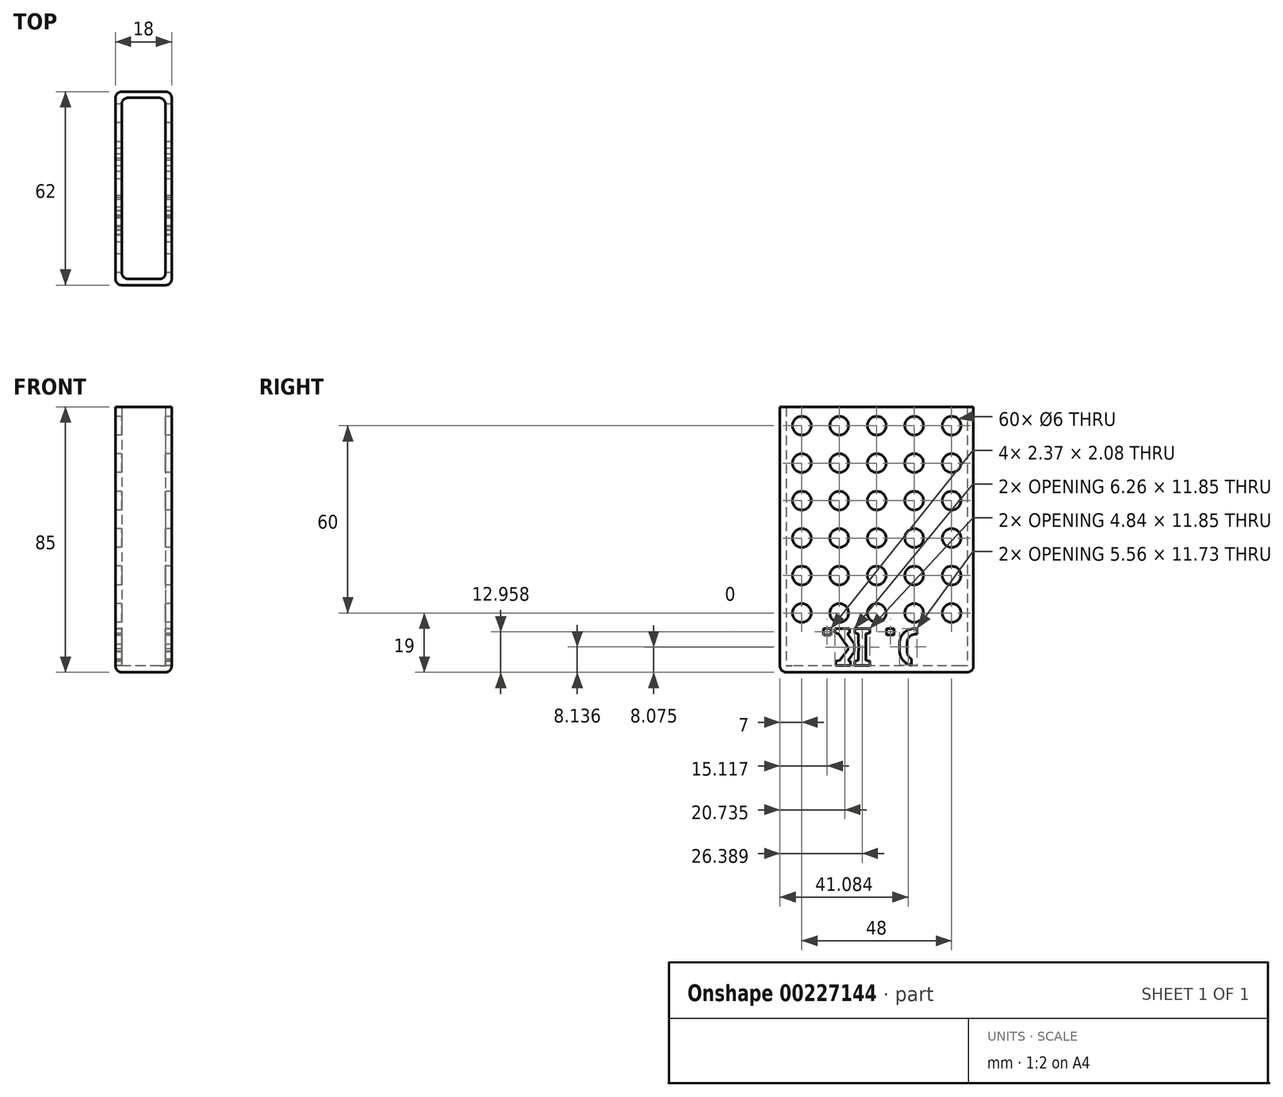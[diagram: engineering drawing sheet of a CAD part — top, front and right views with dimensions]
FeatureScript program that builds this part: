
annotation { "Feature Type Name" : "Feature", "Feature Type Description" : "" }
export const myFeature = defineFeature(function(context is Context, id is Id, definition is map)
    precondition{}
    {
        {
            var Q0;
            Q0=qCreatedBy(makeId("Top.planeOp"),FACE);
            var sketch = newSketch(context, id + "F0", { "sketchPlane" : qUnion([Q0])});
            skLineSegment(sketch, "E0.bottom", {"start": v(7, 31) * mm, "end": v(-7, 31) * mm});
            skLineSegment(sketch, "E0.top", {"start": v(7, -31) * mm, "end": v(-7, -31) * mm});
            skLineSegment(sketch, "E0.left", {"start": v(9, 29) * mm, "end": v(9, -29) * mm});
            skLineSegment(sketch, "E0.right", {"start": v(-9, 29) * mm, "end": v(-9, -29) * mm});
            skPoint(sketch, "E0.middle", {"position": v(0, 0) * mm});
            skPoint(sketch, "E1.visualSharp", {"position": v(9, 31) * mm});
            skArc(sketch, "E1.filletArc", {"start": v(9, 29) * mm, "mid": v(8.41, 30.41) * mm, "end": v(7, 31) * mm});
            skPoint(sketch, "E2.visualSharp", {"position": v(-9, 31) * mm});
            skArc(sketch, "E2.filletArc", {"start": v(-7, 31) * mm, "mid": v(-8.41, 30.41) * mm, "end": v(-9, 29) * mm});
            skPoint(sketch, "E3.visualSharp", {"position": v(-9, -31) * mm});
            skArc(sketch, "E3.filletArc", {"start": v(-9, -29) * mm, "mid": v(-8.41, -30.41) * mm, "end": v(-7, -31) * mm});
            skPoint(sketch, "E4.visualSharp", {"position": v(9, -31) * mm});
            skArc(sketch, "E4.filletArc", {"start": v(7, -31) * mm, "mid": v(8.41, -30.41) * mm, "end": v(9, -29) * mm});
            skLineSegment(sketch, "E5.bottom", {"start": v(5, 29) * mm, "end": v(-5, 29) * mm});
            skLineSegment(sketch, "E5.top", {"start": v(5.2, -29) * mm, "end": v(-5, -29) * mm});
            skLineSegment(sketch, "E5.left", {"start": v(7, 27) * mm, "end": v(7, -27.2) * mm});
            skLineSegment(sketch, "E5.right", {"start": v(-7, 27) * mm, "end": v(-7, -27) * mm});
            skArc(sketch, "E6.filletArc", {"start": v(7, 27) * mm, "mid": v(6.41, 28.41) * mm, "end": v(5, 29) * mm});
            skArc(sketch, "E7.filletArc", {"start": v(-5, 29) * mm, "mid": v(-6.41, 28.41) * mm, "end": v(-7, 27) * mm});
            skArc(sketch, "E8.filletArc", {"start": v(-7, -27) * mm, "mid": v(-6.41, -28.41) * mm, "end": v(-5, -29) * mm});
            skArc(sketch, "E9.filletArc", {"start": v(5.2, -29) * mm, "mid": v(6.47, -28.47) * mm, "end": v(7, -27.2) * mm});
            skSolve(sketch);
        }
        {
            var Q0;
            Q0=makeQuery(id+"F0.imprint","IMPRINT",FACE,{"disambiguationData":[TD([[makeQuery(id+"F0.imprint","IMPRINT",EDGE,{"derivedFrom":sQuery(id+"F0.wireOp",EDGE,"E0.bottom")}),1.0]])]});
            extrude(context, id + "F1", {"entities" : qUnion([Q0]), "depth" : (87 - 4) * mm});
        }
        {
            var Q0;
            Q0=makeQuery(id+"F0.imprint","IMPRINT",FACE,{"disambiguationData":[TD([[makeQuery(id+"F0.imprint","IMPRINT",EDGE,{"derivedFrom":sQuery(id+"F0.wireOp",EDGE,"E0.bottom")}),1.0]])]});
            var Q1;
            Q1=makeQuery(id+"F0.imprint","IMPRINT",FACE,{"disambiguationData":[TD([[makeQuery(id+"F0.imprint","IMPRINT",EDGE,{"derivedFrom":sQuery(id+"F0.wireOp",EDGE,"E5.bottom")}),1.0]])]});
            extrude(context, id + "F2", {"entities" : qUnion([Q0, Q1]), "operationType" : NewBodyOperationType.ADD, "oppositeDirection" : true, "depth" : 2 * mm});
        }
        {
            var Q0;
            Q0=makeQuery(id+"F0.imprint","IMPRINT",FACE,{"disambiguationData":[TD([[makeQuery(id+"F0.imprint","IMPRINT",EDGE,{"derivedFrom":sQuery(id+"F0.wireOp",EDGE,"E0.bottom")}),1.0]])]});
            extrude(context, id + "F3", {"entities" : qUnion([Q0]), "operationType" : NewBodyOperationType.ADD, "oppositeDirection" : true, "depth" : 2 * mm});
        }
        {
            var Q0;
            {var subQ0=sQuery(id+"F0.wireOp",EDGE,"E0.bottom");var subQ1=sQuery(id+"F0.wireOp",EDGE,"E1.filletArc");Q0=makeQuery(id+"FxfuuWBWUbWDivL_1.boolean.opBoolean","SPLIT",EDGE,{"disambiguationData":[TD([makeQuery(id+"F1.opExtrude","SWEPT_FACE",FACE,{"disambiguationData":[OSD([subQ1])]})])],"derivedFrom":makeQuery(id+"F2.opExtrude","CAP_EDGE",EDGE,{"disambiguationData":[OSD([subQ0])],"isStart":false})});}
            fillet(context, id + "F4", {"entities" : qUnion([Q0]), "radius" : 2 * mm, "tangentPropagation" : true, "allowEdgeOverflow" : false});
        }
        {
            var Q0;
            {var subQ0=sQuery(id+"F0.wireOp",EDGE,"E0.right");Q0=makeQuery(id+"F2.boolean.opBoolean","MERGE",FACE,{"derivedFrom":[makeQuery(id+"F1.opExtrude","SWEPT_FACE",FACE,{"disambiguationData":[OSD([subQ0])]}),makeQuery(id+"F2.opExtrude","SWEPT_FACE",FACE,{"disambiguationData":[OSD([subQ0])]})]});}
            var sketch = newSketch(context, id + "F5", { "sketchPlane" : qUnion([Q0])});
            skCircle(sketch, "E10", {"center": v(-24, 77) * mm, "radius": 3 * mm});
            skCircle(sketch, "E11.0.1.0", {"center": v(-24, 65) * mm, "radius": 3 * mm});
            skCircle(sketch, "E11.0.2.0", {"center": v(-24, 53) * mm, "radius": 3 * mm});
            skCircle(sketch, "E11.0.3.0", {"center": v(-24, 41) * mm, "radius": 3 * mm});
            skCircle(sketch, "E11.0.4.0", {"center": v(-24, 29) * mm, "radius": 3 * mm});
            skCircle(sketch, "E11.0.5.0", {"center": v(-24, 17) * mm, "radius": 3 * mm});
            skCircle(sketch, "E11.1.0.0", {"center": v(-12, 77) * mm, "radius": 3 * mm});
            skCircle(sketch, "E11.1.1.0", {"center": v(-12, 65) * mm, "radius": 3 * mm});
            skCircle(sketch, "E11.1.2.0", {"center": v(-12, 53) * mm, "radius": 3 * mm});
            skCircle(sketch, "E11.1.3.0", {"center": v(-12, 41) * mm, "radius": 3 * mm});
            skCircle(sketch, "E11.1.4.0", {"center": v(-12, 29) * mm, "radius": 3 * mm});
            skCircle(sketch, "E11.1.5.0", {"center": v(-12, 17) * mm, "radius": 3 * mm});
            skCircle(sketch, "E11.2.0.0", {"center": v(0, 77) * mm, "radius": 3 * mm});
            skCircle(sketch, "E11.2.1.0", {"center": v(0, 65) * mm, "radius": 3 * mm});
            skCircle(sketch, "E11.2.2.0", {"center": v(0, 53) * mm, "radius": 3 * mm});
            skCircle(sketch, "E11.2.3.0", {"center": v(0, 41) * mm, "radius": 3 * mm});
            skCircle(sketch, "E11.2.4.0", {"center": v(0, 29) * mm, "radius": 3 * mm});
            skCircle(sketch, "E11.2.5.0", {"center": v(0, 17) * mm, "radius": 3 * mm});
            skCircle(sketch, "E11.3.0.0", {"center": v(12, 77) * mm, "radius": 3 * mm});
            skCircle(sketch, "E11.3.1.0", {"center": v(12, 65) * mm, "radius": 3 * mm});
            skCircle(sketch, "E11.3.2.0", {"center": v(12, 53) * mm, "radius": 3 * mm});
            skCircle(sketch, "E11.3.3.0", {"center": v(12, 41) * mm, "radius": 3 * mm});
            skCircle(sketch, "E11.3.4.0", {"center": v(12, 29) * mm, "radius": 3 * mm});
            skCircle(sketch, "E11.3.5.0", {"center": v(12, 17) * mm, "radius": 3 * mm});
            skCircle(sketch, "E11.4.0.0", {"center": v(24, 77) * mm, "radius": 3 * mm});
            skCircle(sketch, "E11.4.1.0", {"center": v(24, 65) * mm, "radius": 3 * mm});
            skCircle(sketch, "E11.4.2.0", {"center": v(24, 53) * mm, "radius": 3 * mm});
            skCircle(sketch, "E11.4.3.0", {"center": v(24, 41) * mm, "radius": 3 * mm});
            skCircle(sketch, "E11.4.4.0", {"center": v(24, 29) * mm, "radius": 3 * mm});
            skCircle(sketch, "E11.4.5.0", {"center": v(24, 17) * mm, "radius": 3 * mm});
            skLineSegment(sketch, "E11.direction1", {"start": v(-24, 77) * mm, "end": v(-12, 77) * mm, "construction": true});
            skLineSegment(sketch, "E11.direction2", {"start": v(-24, 77) * mm, "end": v(-24, 65) * mm, "construction": true});
            skSolve(sketch);
        }
        {
            var Q0;
            Q0=makeQuery(id+"F5.imprint","IMPRINT",FACE,{"disambiguationData":[TD([[makeQuery(id+"F5.imprint","IMPRINT",EDGE,{"derivedFrom":sQuery(id+"F5.wireOp",EDGE,"E10")}),1.0]])]});
            var Q1;
            Q1=makeQuery(id+"F5.imprint","IMPRINT",FACE,{"disambiguationData":[TD([[makeQuery(id+"F5.imprint","IMPRINT",EDGE,{"derivedFrom":sQuery(id+"F5.wireOp",EDGE,"E11.0.5.0")}),1.0]])]});
            var Q2;
            Q2=makeQuery(id+"F5.imprint","IMPRINT",FACE,{"disambiguationData":[TD([[makeQuery(id+"F5.imprint","IMPRINT",EDGE,{"derivedFrom":sQuery(id+"F5.wireOp",EDGE,"E11.1.5.0")}),1.0]])]});
            var Q3;
            Q3=makeQuery(id+"F5.imprint","IMPRINT",FACE,{"disambiguationData":[TD([[makeQuery(id+"F5.imprint","IMPRINT",EDGE,{"derivedFrom":sQuery(id+"F5.wireOp",EDGE,"E11.2.5.0")}),1.0]])]});
            var Q4;
            Q4=makeQuery(id+"F5.imprint","IMPRINT",FACE,{"disambiguationData":[TD([[makeQuery(id+"F5.imprint","IMPRINT",EDGE,{"derivedFrom":sQuery(id+"F5.wireOp",EDGE,"E11.4.5.0")}),1.0]])]});
            var Q5;
            Q5=makeQuery(id+"F5.imprint","IMPRINT",FACE,{"disambiguationData":[TD([[makeQuery(id+"F5.imprint","IMPRINT",EDGE,{"derivedFrom":sQuery(id+"F5.wireOp",EDGE,"E11.4.4.0")}),1.0]])]});
            var Q6;
            Q6=makeQuery(id+"F5.imprint","IMPRINT",FACE,{"disambiguationData":[TD([[makeQuery(id+"F5.imprint","IMPRINT",EDGE,{"derivedFrom":sQuery(id+"F5.wireOp",EDGE,"E11.4.3.0")}),1.0]])]});
            var Q7;
            Q7=makeQuery(id+"F5.imprint","IMPRINT",FACE,{"disambiguationData":[TD([[makeQuery(id+"F5.imprint","IMPRINT",EDGE,{"derivedFrom":sQuery(id+"F5.wireOp",EDGE,"E11.4.2.0")}),1.0]])]});
            var Q8;
            Q8=makeQuery(id+"F5.imprint","IMPRINT",FACE,{"disambiguationData":[TD([[makeQuery(id+"F5.imprint","IMPRINT",EDGE,{"derivedFrom":sQuery(id+"F5.wireOp",EDGE,"E11.4.1.0")}),1.0]])]});
            var Q9;
            Q9=makeQuery(id+"F5.imprint","IMPRINT",FACE,{"disambiguationData":[TD([[makeQuery(id+"F5.imprint","IMPRINT",EDGE,{"derivedFrom":sQuery(id+"F5.wireOp",EDGE,"E11.4.0.0")}),1.0]])]});
            var Q10;
            Q10=makeQuery(id+"F5.imprint","IMPRINT",FACE,{"disambiguationData":[TD([[makeQuery(id+"F5.imprint","IMPRINT",EDGE,{"derivedFrom":sQuery(id+"F5.wireOp",EDGE,"E11.2.0.0")}),1.0]])]});
            var Q11;
            Q11=makeQuery(id+"F5.imprint","IMPRINT",FACE,{"disambiguationData":[TD([[makeQuery(id+"F5.imprint","IMPRINT",EDGE,{"derivedFrom":sQuery(id+"F5.wireOp",EDGE,"E11.1.0.0")}),1.0]])]});
            var Q12;
            Q12=makeQuery(id+"F5.imprint","IMPRINT",FACE,{"disambiguationData":[TD([[makeQuery(id+"F5.imprint","IMPRINT",EDGE,{"derivedFrom":sQuery(id+"F5.wireOp",EDGE,"E11.3.1.0")}),1.0]])]});
            var Q13;
            Q13=makeQuery(id+"F5.imprint","IMPRINT",FACE,{"disambiguationData":[TD([[makeQuery(id+"F5.imprint","IMPRINT",EDGE,{"derivedFrom":sQuery(id+"F5.wireOp",EDGE,"E11.3.0.0")}),1.0]])]});
            var Q14;
            Q14=makeQuery(id+"F5.imprint","IMPRINT",FACE,{"disambiguationData":[TD([[makeQuery(id+"F5.imprint","IMPRINT",EDGE,{"derivedFrom":sQuery(id+"F5.wireOp",EDGE,"E11.3.2.0")}),1.0]])]});
            var Q15;
            Q15=makeQuery(id+"F5.imprint","IMPRINT",FACE,{"disambiguationData":[TD([[makeQuery(id+"F5.imprint","IMPRINT",EDGE,{"derivedFrom":sQuery(id+"F5.wireOp",EDGE,"E11.3.3.0")}),1.0]])]});
            var Q16;
            Q16=makeQuery(id+"F5.imprint","IMPRINT",FACE,{"disambiguationData":[TD([[makeQuery(id+"F5.imprint","IMPRINT",EDGE,{"derivedFrom":sQuery(id+"F5.wireOp",EDGE,"E11.3.4.0")}),1.0]])]});
            var Q17;
            Q17=makeQuery(id+"F5.imprint","IMPRINT",FACE,{"disambiguationData":[TD([[makeQuery(id+"F5.imprint","IMPRINT",EDGE,{"derivedFrom":sQuery(id+"F5.wireOp",EDGE,"E11.3.5.0")}),1.0]])]});
            var Q18;
            Q18=makeQuery(id+"F5.imprint","IMPRINT",FACE,{"disambiguationData":[TD([[makeQuery(id+"F5.imprint","IMPRINT",EDGE,{"derivedFrom":sQuery(id+"F5.wireOp",EDGE,"E11.2.4.0")}),1.0]])]});
            var Q19;
            Q19=makeQuery(id+"F5.imprint","IMPRINT",FACE,{"disambiguationData":[TD([[makeQuery(id+"F5.imprint","IMPRINT",EDGE,{"derivedFrom":sQuery(id+"F5.wireOp",EDGE,"E11.2.3.0")}),1.0]])]});
            var Q20;
            Q20=makeQuery(id+"F5.imprint","IMPRINT",FACE,{"disambiguationData":[TD([[makeQuery(id+"F5.imprint","IMPRINT",EDGE,{"derivedFrom":sQuery(id+"F5.wireOp",EDGE,"E11.2.2.0")}),1.0]])]});
            var Q21;
            Q21=makeQuery(id+"F5.imprint","IMPRINT",FACE,{"disambiguationData":[TD([[makeQuery(id+"F5.imprint","IMPRINT",EDGE,{"derivedFrom":sQuery(id+"F5.wireOp",EDGE,"E11.2.1.0")}),1.0]])]});
            var Q22;
            Q22=makeQuery(id+"F5.imprint","IMPRINT",FACE,{"disambiguationData":[TD([[makeQuery(id+"F5.imprint","IMPRINT",EDGE,{"derivedFrom":sQuery(id+"F5.wireOp",EDGE,"E11.1.1.0")}),1.0]])]});
            var Q23;
            Q23=makeQuery(id+"F5.imprint","IMPRINT",FACE,{"disambiguationData":[TD([[makeQuery(id+"F5.imprint","IMPRINT",EDGE,{"derivedFrom":sQuery(id+"F5.wireOp",EDGE,"E11.0.1.0")}),1.0]])]});
            var Q24;
            Q24=makeQuery(id+"F5.imprint","IMPRINT",FACE,{"disambiguationData":[TD([[makeQuery(id+"F5.imprint","IMPRINT",EDGE,{"derivedFrom":sQuery(id+"F5.wireOp",EDGE,"E11.0.2.0")}),1.0]])]});
            var Q25;
            Q25=makeQuery(id+"F5.imprint","IMPRINT",FACE,{"disambiguationData":[TD([[makeQuery(id+"F5.imprint","IMPRINT",EDGE,{"derivedFrom":sQuery(id+"F5.wireOp",EDGE,"E11.1.2.0")}),1.0]])]});
            var Q26;
            Q26=makeQuery(id+"F5.imprint","IMPRINT",FACE,{"disambiguationData":[TD([[makeQuery(id+"F5.imprint","IMPRINT",EDGE,{"derivedFrom":sQuery(id+"F5.wireOp",EDGE,"E11.1.3.0")}),1.0]])]});
            var Q27;
            Q27=makeQuery(id+"F5.imprint","IMPRINT",FACE,{"disambiguationData":[TD([[makeQuery(id+"F5.imprint","IMPRINT",EDGE,{"derivedFrom":sQuery(id+"F5.wireOp",EDGE,"E11.0.3.0")}),1.0]])]});
            var Q28;
            Q28=makeQuery(id+"F5.imprint","IMPRINT",FACE,{"disambiguationData":[TD([[makeQuery(id+"F5.imprint","IMPRINT",EDGE,{"derivedFrom":sQuery(id+"F5.wireOp",EDGE,"E11.0.4.0")}),1.0]])]});
            var Q29;
            Q29=makeQuery(id+"F5.imprint","IMPRINT",FACE,{"disambiguationData":[TD([[makeQuery(id+"F5.imprint","IMPRINT",EDGE,{"derivedFrom":sQuery(id+"F5.wireOp",EDGE,"E11.1.4.0")}),1.0]])]});
            extrude(context, id + "F6", {"entities" : qUnion([Q0, Q1, Q2, Q3, Q4, Q5, Q6, Q7, Q8, Q9, Q10, Q11, Q12, Q13, Q14, Q15, Q16, Q17, Q18, Q19, Q20, Q21, Q22, Q23, Q24, Q25, Q26, Q27, Q28, Q29]), "operationType" : NewBodyOperationType.REMOVE, "endBound" : BoundingType.THROUGH_ALL, "oppositeDirection" : true, "depth" : 25 * mm});
        }
        {
            var Q0;
            {var subQ0=sQuery(id+"F0.wireOp",EDGE,"E0.left");Q0=makeQuery(id+"F2.boolean.opBoolean","MERGE",FACE,{"derivedFrom":[makeQuery(id+"F1.opExtrude","SWEPT_FACE",FACE,{"disambiguationData":[OSD([subQ0])]}),makeQuery(id+"F2.opExtrude","SWEPT_FACE",FACE,{"disambiguationData":[OSD([subQ0])]})]});}
            var sketch = newSketch(context, id + "F7", { "sketchPlane" : qUnion([Q0])});
            skText(sketch, "E12", { "text": "D. K.", "fontName": "RobotoSlab-Bold.ttf"});
            skLineSegment(sketch, "E13", {"start": v(24, 14) * mm, "end": v(-24, 14) * mm, "construction": true});
            skLineSegment(sketch, "E14", {"start": v(12.86, 12) * mm, "end": v(12.86, 0) * mm});
            skLineSegment(sketch, "E15", {"start": v(12.86, 0) * mm, "end": v(11.08, 0) * mm});
            skLineSegment(sketch, "E16", {"start": v(11.08, 0) * mm, "end": v(11.08, 12) * mm});
            skLineSegment(sketch, "E17", {"start": v(11.08, 12) * mm, "end": v(12.86, 12) * mm});
            skLineSegment(sketch, "E18", {"start": v(-5.82, 4.87) * mm, "end": v(-5.82, 7.07) * mm});
            skLineSegment(sketch, "E19", {"start": v(-5.82, 7.07) * mm, "end": v(-7.14, 7.07) * mm});
            skLineSegment(sketch, "E20", {"start": v(-7.14, 7.07) * mm, "end": v(-7.14, 4.6) * mm});
            skLineSegment(sketch, "E21", {"start": v(-7.14, 4.6) * mm, "end": v(-5.82, 4.87) * mm});
            const initialGuessF7  = {"E12": [0.01808, 0.012, -1, 0, 0.012]};
            skSetInitialGuess(sketch, initialGuessF7);
            skSolve(sketch);
        }
        {
            var Q0;
            {var subQ1=sQuery(id+"F7.wireOp",EDGE,"E12.sketch_text.stroke-1");Q0=makeQuery(id+"F7.imprint","IMPRINT",FACE,{"disambiguationData":[TD([[makeQuery(id+"F7.imprint","IMPRINT",EDGE,{"derivedFrom":subQ1}),-1.0]])]});}
            var Q1;
            {var subQ7=sQuery(id+"F7.wireOp",EDGE,"E12.sketch_text.stroke-5");Q1=makeQuery(id+"F7.imprint","IMPRINT",FACE,{"disambiguationData":[TD([[makeQuery(id+"F7.imprint","IMPRINT",EDGE,{"derivedFrom":subQ7}),-1.0]])]});}
            var Q2;
            Q2=makeQuery(id+"F7.imprint","IMPRINT",FACE,{"disambiguationData":[TD([[makeQuery(id+"F7.imprint","IMPRINT",EDGE,{"derivedFrom":sQuery(id+"F7.wireOp",EDGE,"E12.sketch_text.stroke-21")}),-1.0]])]});
            var Q3;
            Q3=makeQuery(id+"F7.imprint","IMPRINT",FACE,{"disambiguationData":[TD([[makeQuery(id+"F7.imprint","IMPRINT",EDGE,{"derivedFrom":sQuery(id+"F7.wireOp",EDGE,"E12.sketch_text.stroke-25")}),-1.0]])]});
            var Q4;
            Q4=makeQuery(id+"F7.imprint","IMPRINT",FACE,{"disambiguationData":[TD([[makeQuery(id+"F7.imprint","IMPRINT",EDGE,{"derivedFrom":sQuery(id+"F7.wireOp",EDGE,"E12.sketch_text.stroke-54")}),-1.0]])]});
            var Q5;
            {var subQ4=sQuery(id+"F7.wireOp",EDGE,"E12.sketch_text.stroke-35");Q5=makeQuery(id+"F7.imprint","IMPRINT",FACE,{"disambiguationData":[TD([[makeQuery(id+"F7.imprint","IMPRINT",EDGE,{"derivedFrom":subQ4}),-1.0]])]});}
            extrude(context, id + "F8", {"entities" : qUnion([Q0, Q1, Q2, Q3, Q4, Q5]), "operationType" : NewBodyOperationType.REMOVE, "endBound" : BoundingType.THROUGH_ALL, "oppositeDirection" : true, "depth" : 25 * mm});
        }
    });
